# Revit family: Haworth_Compose_Panel_StackGlass
name_source: partatom
category: Furniture Systems
revit_build: Autodesk Revit 2018 (Build: 20170223_1515(x64)
units: mm (PartAtom-declared; Revit-internal decimal feet)

## family parameters
Always vertical = Yes
Cut with Voids When Loaded = No
OmniClass Number = 23.40.70.14.64.21
OmniClass Title = Systems Furniture
Part Type = Normal
Room Calculation Point = No
Round Connector Dimension = Use Diameter
Shared = No
Work Plane-Based = No

## types (28) — shared parameters
Adjacent Panel Height Left = 8"
Adjacent Panel Height Right = 8"
Assembly Code = E2020500
Custom Size = No
Description = Haworth - Compose Panel Glass - Stack
Frame Depth = 2 3/4"
Frame Width = 3/4"
Glass Finish = Haworth _ Glass _ Clear
Manufacturer = Haworth
Max. Height = 24"
Max. Width = 96"
Min. Height = 16"
Min. Width = 18"
Min/Max Height = 16, 24 in.
Min/Max Width = 18-96 in. @ 6 in. Increments
Model = VZGS
Panel Depth = 1/2"
Revision Number = 5
Size = Verify Final Dim. w/ Haworth
Sustainability Info = http://media.haworth.com
Top Trim = Yes
Top Trim Adjuster = 1/8"
Top Trim Width = 1/8"
Trim Depth = 3"
Trim Finish = Haworth _ Metal _ Brushed Aluminum
Trim Thin Profile = Yes
URL = www.haworth.com
URL - Product = http://www.haworth.com
Vertical Trim Width = 1/4"
Warranty = http://www.haworth.com

## per-type parameters (varying)
| type | Actual Height | Actual Width | Height | Panel Height | Panel Width | Width |
| 16h 18w | 15 7/8" | 18" | 16" | 14 1/4" | 16 1/2" | 18" |
| 16h 24w | 15 7/8" | 24" | 16" | 14 1/4" | 22 1/2" | 24" |
| 16h 30w | 15 7/8" | 30" | 16" | 14 1/4" | 28 1/2" | 30" |
| 16h 36w | 15 7/8" | 36" | 16" | 14 1/4" | 34 1/2" | 36" |
| 16h 42w | 15 7/8" | 42" | 16" | 14 1/4" | 40 1/2" | 42" |
| 16h 48w | 15 7/8" | 48" | 16" | 14 1/4" | 46 1/2" | 48" |
| 16h 54w | 15 7/8" | 54" | 16" | 14 1/4" | 52 1/2" | 54" |
| 16h 60w | 15 7/8" | 60" | 16" | 14 1/4" | 58 1/2" | 60" |
| 16h 66w | 15 7/8" | 66" | 16" | 14 1/4" | 64 1/2" | 66" |
| 16h 72w | 15 7/8" | 72" | 16" | 14 1/4" | 70 1/2" | 72" |
| 16h 78w | 15 7/8" | 78" | 16" | 14 1/4" | 76 1/2" | 78" |
| 16h 84w | 15 7/8" | 84" | 16" | 14 1/4" | 82 1/2" | 84" |
| 16h 90w | 15 7/8" | 90" | 16" | 14 1/4" | 88 1/2" | 90" |
| 16h 96w | 15 7/8" | 96" | 16" | 14 1/4" | 94 1/2" | 96" |
| 24h 18w | 23 7/8" | 18" | 24" | 22 1/4" | 16 1/2" | 18" |
| 24h 24w | 23 7/8" | 24" | 24" | 22 1/4" | 22 1/2" | 24" |
| 24h 30w | 23 7/8" | 30" | 24" | 22 1/4" | 28 1/2" | 30" |
| 24h 36w | 23 7/8" | 36" | 24" | 22 1/4" | 34 1/2" | 36" |
| 24h 42w | 23 7/8" | 42" | 24" | 22 1/4" | 40 1/2" | 42" |
| 24h 48w | 23 7/8" | 48" | 24" | 22 1/4" | 46 1/2" | 48" |
| 24h 54w | 23 7/8" | 54" | 24" | 22 1/4" | 52 1/2" | 54" |
| 24h 60w | 23 7/8" | 60" | 24" | 22 1/4" | 58 1/2" | 60" |
| 24h 66w | 23 7/8" | 66" | 24" | 22 1/4" | 64 1/2" | 66" |
| 24h 72w | 23 7/8" | 72" | 24" | 22 1/4" | 70 1/2" | 72" |
| 24h 78w | 23 7/8" | 78" | 24" | 22 1/4" | 76 1/2" | 78" |
| 24h 84w | 23 7/8" | 84" | 24" | 22 1/4" | 82 1/2" | 84" |
| 24h 90w | 23 7/8" | 90" | 24" | 22 1/4" | 88 1/2" | 90" |
| 24h 96w | 23 7/8" | 96" | 24" | 22 1/4" | 94 1/2" | 96" |

## geometry (parser evidence)
native form markers: Sweep x9
no freeform markers — native parametric forms only
